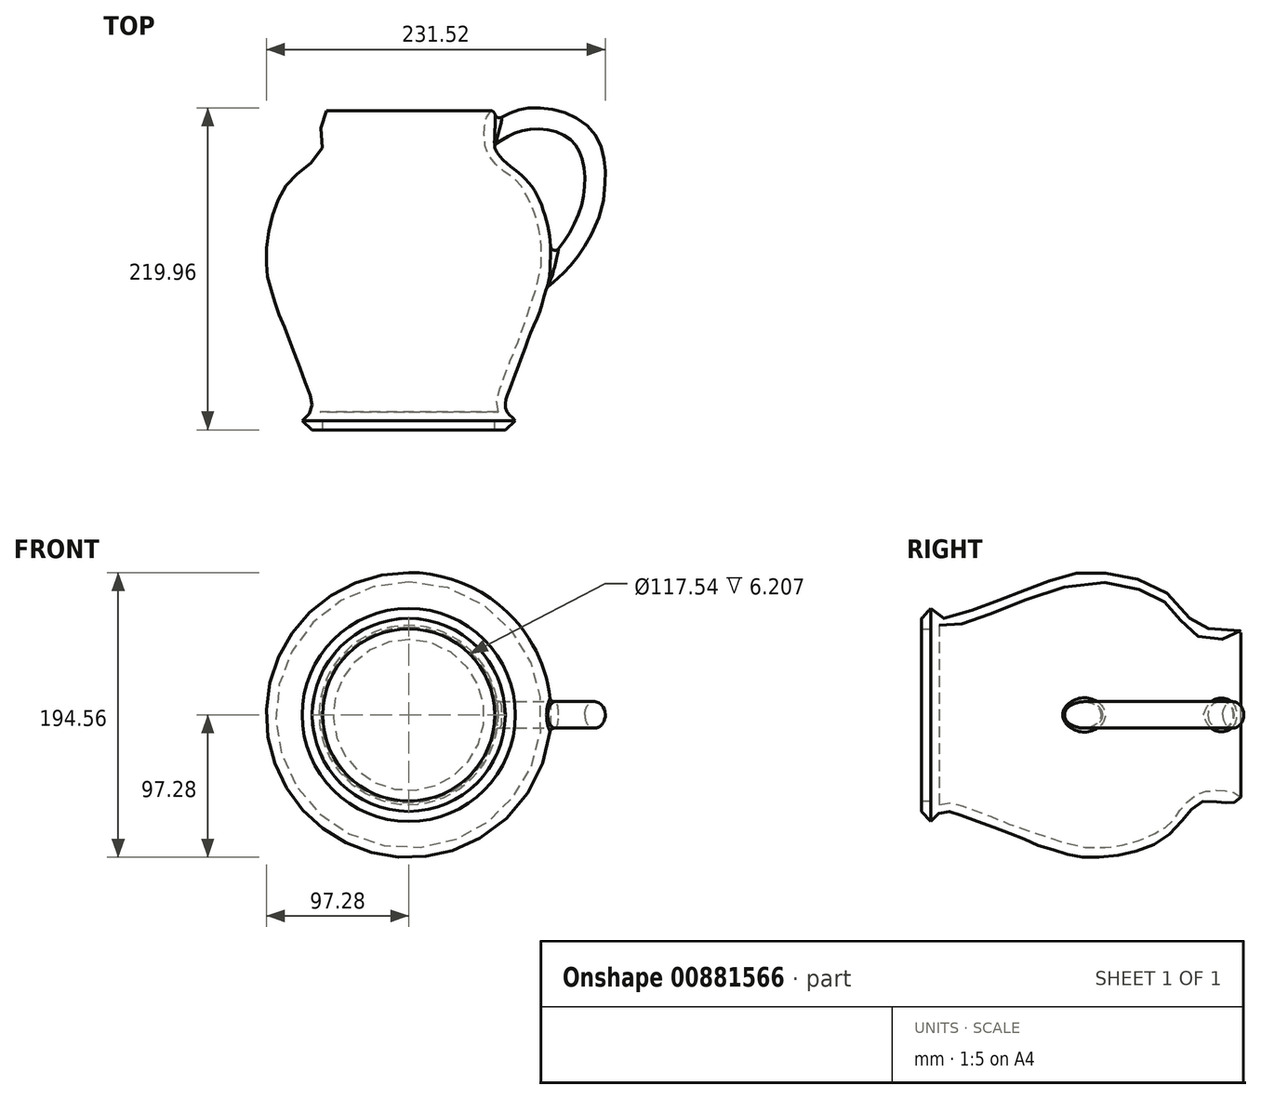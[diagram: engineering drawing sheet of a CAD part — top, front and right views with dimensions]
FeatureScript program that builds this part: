
annotation { "Feature Type Name" : "Feature", "Feature Type Description" : "" }
export const myFeature = defineFeature(function(context is Context, id is Id, definition is map)
    precondition{}
    {
        {
            var Q0;
            Q0=qCreatedBy(makeId("Top.planeOp"),FACE);
            var sketch = newSketch(context, id + "F0", { "sketchPlane" : qUnion([Q0])});
            skLineSegment(sketch, "E0", {"start": v(219.22, -22.72) * mm, "end": v(219.22, -28.92) * mm});
            skLineSegment(sketch, "E1", {"start": v(219.22, -28.92) * mm, "end": v(226.35, -28.92) * mm});
            skLineSegment(sketch, "E2", {"start": v(226.35, -28.92) * mm, "end": v(233.26, -22.72) * mm});
            skLineSegment(sketch, "E3", {"start": v(221.64, -16.85) * mm, "end": v(160.45, -16.85) * mm});
            skLineSegment(sketch, "E4", {"start": v(160.45, -16.85) * mm, "end": v(160.45, -22.72) * mm});
            skLineSegment(sketch, "E5", {"start": v(160.45, -22.72) * mm, "end": v(219.22, -22.72) * mm});
            skPoint(sketch, "E6.1.internal.snap0", {"position": v(229.8, -25.82) * mm});
            skFitSpline(sketch, "E6", {"points": [v(233.26, -22.72) * mm, v(229.8, -19.12) * mm, v(227.4, -16.51) * mm, v(226.36, -10.9) * mm, v(230.93, 3.04) * mm, v(237.44, 20.51) * mm, v(239.66, 26) * mm, v(244.61, 39.55) * mm, v(249.17, 49.72) * mm, v(252.04, 59.1) * mm, v(256.73, 74.23) * mm, v(257.52, 78.93) * mm, v(257.51, 95.1) * mm, v(254.9, 112.31) * mm, v(249.42, 128.74) * mm, v(240.3, 142.31) * mm, v(225.95, 154.58) * mm, v(219.42, 162.93) * mm, v(219.42, 166.58) * mm, v(219.68, 185.88) * mm, v(216.03, 189.01) * mm, v(212.64, 180.93) * mm, v(212.12, 170.5) * mm, v(213.69, 161.1) * mm, v(217.86, 154.58) * mm, v(225.42, 147.54) * mm, v(233.26, 142.32) * mm, v(238.99, 134.75) * mm, v(244.99, 122.75) * mm, v(249.69, 107.1) * mm, v(250.73, 81.8) * mm, v(243.7, 56.24) * mm, v(235.61, 32.51) * mm, v(227.27, 11.91) * mm, v(223.1, 0) * mm, v(220.28, -9.28) * mm, v(221.64, -16.85) * mm], "startDerivative": vector(-197.96, 214.65) * mm, "endDerivative": vector(103.64, -332.93) * mm});
            skSolve(sketch);
        }
        {
            var Q0;
            Q0=qCreatedBy(makeId("Top.planeOp"),FACE);
            var sketch = newSketch(context, id + "F1", { "sketchPlane" : qUnion([Q0])});
            skLineSegment(sketch, "E7", {"start": v(250.3, 62.93) * mm, "end": v(254.17, 85.43) * mm});
            skLineSegment(sketch, "E8", {"start": v(216.53, 164.03) * mm, "end": v(216.53, 179.67) * mm});
            skFitSpline(sketch, "E9", {"points": [v(216.53, 164.03) * mm, v(226.3, 170.52) * mm, v(237.87, 175.56) * mm, v(255.64, 176.14) * mm, v(270.75, 169.56) * mm, v(278.31, 158.29) * mm, v(280.71, 139) * mm, v(276.37, 118.07) * mm, v(264.26, 96.54) * mm, v(254.17, 85.43) * mm], "startDerivative": vector(103.38, 72.3) * mm, "endDerivative": vector(-94.46, -93.2) * mm});
            skFitSpline(sketch, "E10", {"points": [v(250.3, 62.93) * mm, v(254.17, 62.93) * mm, v(275.87, 90.14) * mm, v(288.07, 111.35) * mm, v(296.26, 145.75) * mm, v(290.49, 170.47) * mm, v(273.8, 187.96) * mm, v(254.17, 193.02) * mm, v(216.53, 179.67) * mm], "startDerivative": vector(66.6, -26.75) * mm, "endDerivative": vector(-253.35, -116.2) * mm});
            skSolve(sketch);
        }
        {
            var Q0;
            Q0=makeQuery(id+"F0.imprint","IMPRINT",FACE,{"disambiguationData":[TD([[makeQuery(id+"F0.imprint","IMPRINT",EDGE,{"derivedFrom":sQuery(id+"F0.wireOp",EDGE,"E0")}),1.0]])]});
            var Q1;
            Q1=sQuery(id+"F0.wireOp",EDGE,"E4");
            revolve(context, id + "F2", {"surfaceOperationType" : NewSurfaceOperationType.NEW, "entities" : qUnion([Q0]), "axis" : qUnion([Q1]), "revolveType" : RevolveType.FULL});
        }
        {
            var Q0;
            Q0=qCreatedBy(makeId("Right.planeOp"),FACE);
            cPlane(context, id + "F3", {"entities" : qUnion([Q0]), "cplaneType" : CPlaneType.OFFSET, "offset" : 255 * mm, "width" : 150 * mm, "height" : 150 * mm});
        }
        {
            var Q0;
            Q0=qCreatedBy(id+"F3.planeOp",FACE);
            var sketch = newSketch(context, id + "F4", { "sketchPlane" : qUnion([Q0])});
            skCircle(sketch, "E11", {"center": v(77.3, 0) * mm, "radius": 9.05 * mm});
            skSolve(sketch);
        }
        {
            var Q0;
            Q0 = qSketchRegion(id + "F4", true);
            var Q1;
            Q1=sQuery(id+"F1.wireOp",EDGE,"E9");
            sweep(context, id + "F5", {"operationType" : NewBodyOperationType.ADD, "profiles" : qUnion([Q0]), "path" : qUnion([Q1])});
        }
        {
            var Q0;
            Q0=makeQuery(id+"F5.boolean.opBoolean","INTERSECT",EDGE,{"disambiguationData":[OD(0.0)],"derivedFrom":[makeQuery(id+"F2.opRevolve","SWEPT_FACE",FACE,{"disambiguationData":[OSD([sQuery(id+"F0.wireOp",EDGE,"E6")])]}),makeQuery(id+"F5.opSweep","SWEPT_FACE",FACE,{"disambiguationData":[OSD([sQuery(id+"F1.wireOp",EDGE,"E9"),sQuery(id+"F4.wireOp",EDGE,"E11")])]})]});
            var Q1;
            Q1=makeQuery(id+"F5.boolean.opBoolean","INTERSECT",EDGE,{"disambiguationData":[OD(1.0)],"derivedFrom":[makeQuery(id+"F2.opRevolve","SWEPT_FACE",FACE,{"disambiguationData":[OSD([sQuery(id+"F0.wireOp",EDGE,"E6")])]}),makeQuery(id+"F5.opSweep","SWEPT_FACE",FACE,{"disambiguationData":[OSD([sQuery(id+"F1.wireOp",EDGE,"E9"),sQuery(id+"F4.wireOp",EDGE,"E11")])]})]});
            fillet(context, id + "F6", {"entities" : qUnion([Q0, Q1]), "radius" : 3 * mm, "tangentPropagation" : true, "allowEdgeOverflow" : false});
        }
    });
